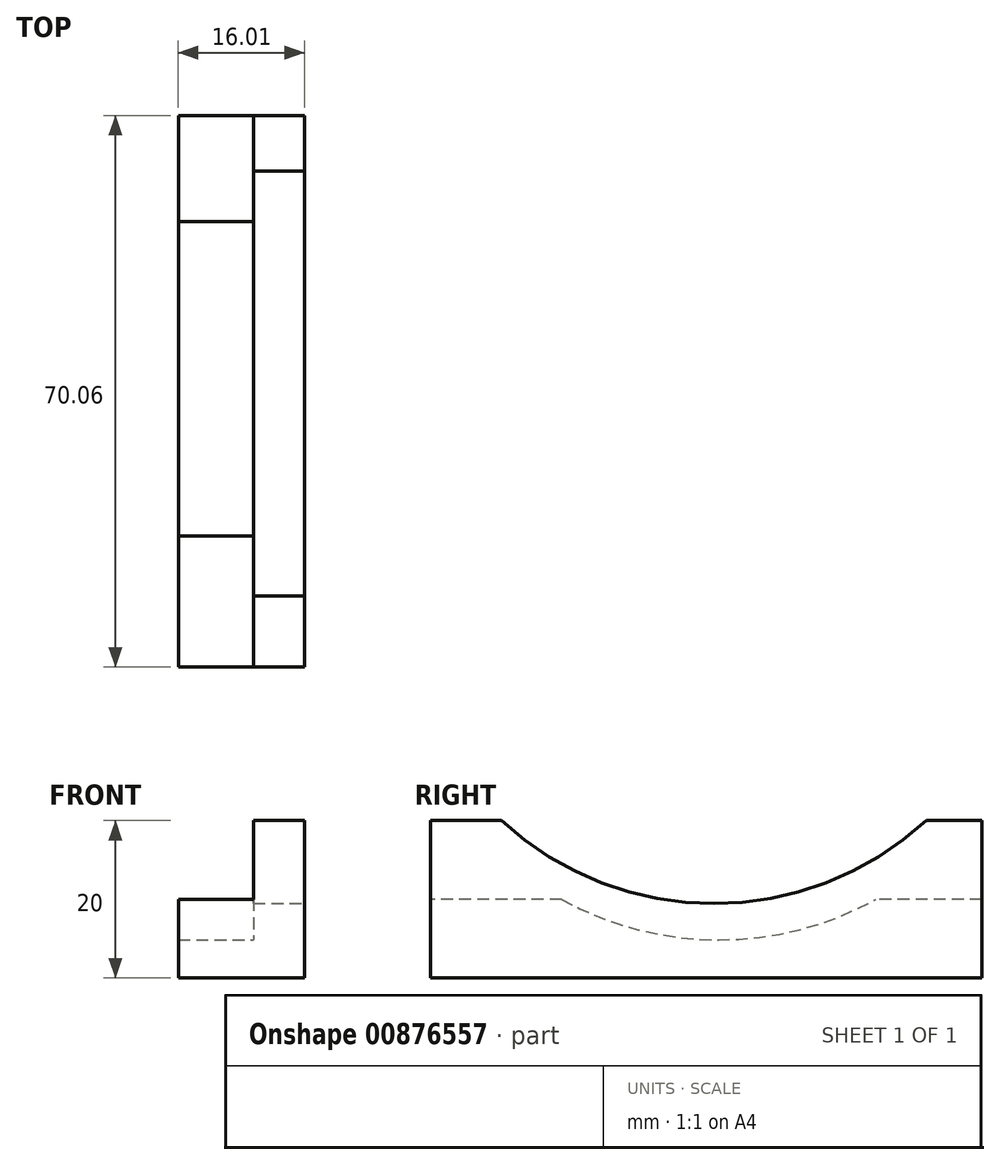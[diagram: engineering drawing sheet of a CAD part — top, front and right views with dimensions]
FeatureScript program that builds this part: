
annotation { "Feature Type Name" : "Feature", "Feature Type Description" : "" }
export const myFeature = defineFeature(function(context is Context, id is Id, definition is map)
    precondition{}
    {
        {
            var Q0;
            Q0=qCreatedBy(makeId("Top.planeOp"),FACE);
            var sketch = newSketch(context, id + "F0", { "sketchPlane" : qUnion([Q0])});
            skLineSegment(sketch, "E0.bottom", {"start": v(-45.19, 47.27) * mm, "end": v(-35.64, 47.27) * mm});
            skLineSegment(sketch, "E0.top", {"start": v(-45.19, -22.79) * mm, "end": v(-35.64, -22.79) * mm});
            skLineSegment(sketch, "E0.left", {"start": v(-45.19, 47.27) * mm, "end": v(-45.19, -22.79) * mm});
            skLineSegment(sketch, "E0.right", {"start": v(-35.64, 47.27) * mm, "end": v(-35.64, -22.79) * mm});
            skLineSegment(sketch, "E1", {"start": v(-35.64, 47.27) * mm, "end": v(-29.18, 47.27) * mm});
            skLineSegment(sketch, "E2", {"start": v(-29.18, 47.27) * mm, "end": v(-29.18, -22.79) * mm});
            skLineSegment(sketch, "E3", {"start": v(-29.18, -22.79) * mm, "end": v(-35.64, -22.79) * mm});
            skSolve(sketch);
        }
        {
            var Q0;
            Q0=makeQuery(id+"F0.imprint","IMPRINT",FACE,{"disambiguationData":[TD([[makeQuery(id+"F0.imprint","IMPRINT",EDGE,{"derivedFrom":sQuery(id+"F0.wireOp",EDGE,"E0.bottom")}),-1.0]])]});
            extrude(context, id + "F1", {"entities" : qUnion([Q0]), "depth" : 10 * mm, "offsetDistance" : 25 * mm});
        }
        {
            var Q0;
            Q0=qCreatedBy(makeId("Right.planeOp"),FACE);
            var sketch = newSketch(context, id + "F2", { "sketchPlane" : qUnion([Q0])});
            skLineSegment(sketch, "E4", {"start": v(39.21, 13.58) * mm, "end": v(-10.67, 12.94) * mm});
            skArc(sketch, "E5", {"start": v(-10.67, 12.94) * mm, "mid": v(14.38, 4.83) * mm, "end": v(39.21, 13.58) * mm});
            skSolve(sketch);
        }
        {
            var Q0;
            Q0 = qSketchRegion(id + "F2", true);
            extrude(context, id + "F3", {"entities" : qUnion([Q0]), "operationType" : NewBodyOperationType.REMOVE, "oppositeDirection" : true, "depth" : 50 * mm, "offsetDistance" : 25 * mm});
        }
        {
            var Q0;
            Q0=makeQuery(id+"F0.imprint","IMPRINT",FACE,{"disambiguationData":[TD([[makeQuery(id+"F0.imprint","IMPRINT",EDGE,{"derivedFrom":sQuery(id+"F0.wireOp",EDGE,"E0.right")}),1.0]])]});
            extrude(context, id + "F4", {"entities" : qUnion([Q0]), "operationType" : NewBodyOperationType.ADD, "depth" : 20 * mm, "offsetDistance" : 25 * mm});
        }
        {
            var Q0;
            Q0=qCreatedBy(makeId("Right.planeOp"),FACE);
            var sketch = newSketch(context, id + "F5", { "sketchPlane" : qUnion([Q0])});
            skArc(sketch, "E6", {"start": v(-19.58, 26.72) * mm, "mid": v(13.2, 9.46) * mm, "end": v(46, 26.7) * mm});
            skLineSegment(sketch, "E7", {"start": v(-19.58, 26.72) * mm, "end": v(46, 26.7) * mm});
            skSolve(sketch);
        }
        {
            var Q0;
            Q0=makeQuery(id+"F5.imprint","IMPRINT",FACE,{"disambiguationData":[TD([[makeQuery(id+"F5.imprint","IMPRINT",EDGE,{"derivedFrom":sQuery(id+"F5.wireOp",EDGE,"E6")}),1.0]])]});
            extrude(context, id + "F6", {"entities" : qUnion([Q0]), "operationType" : NewBodyOperationType.REMOVE, "oppositeDirection" : true, "depth" : 50 * mm, "offsetDistance" : 25 * mm});
        }
    });
